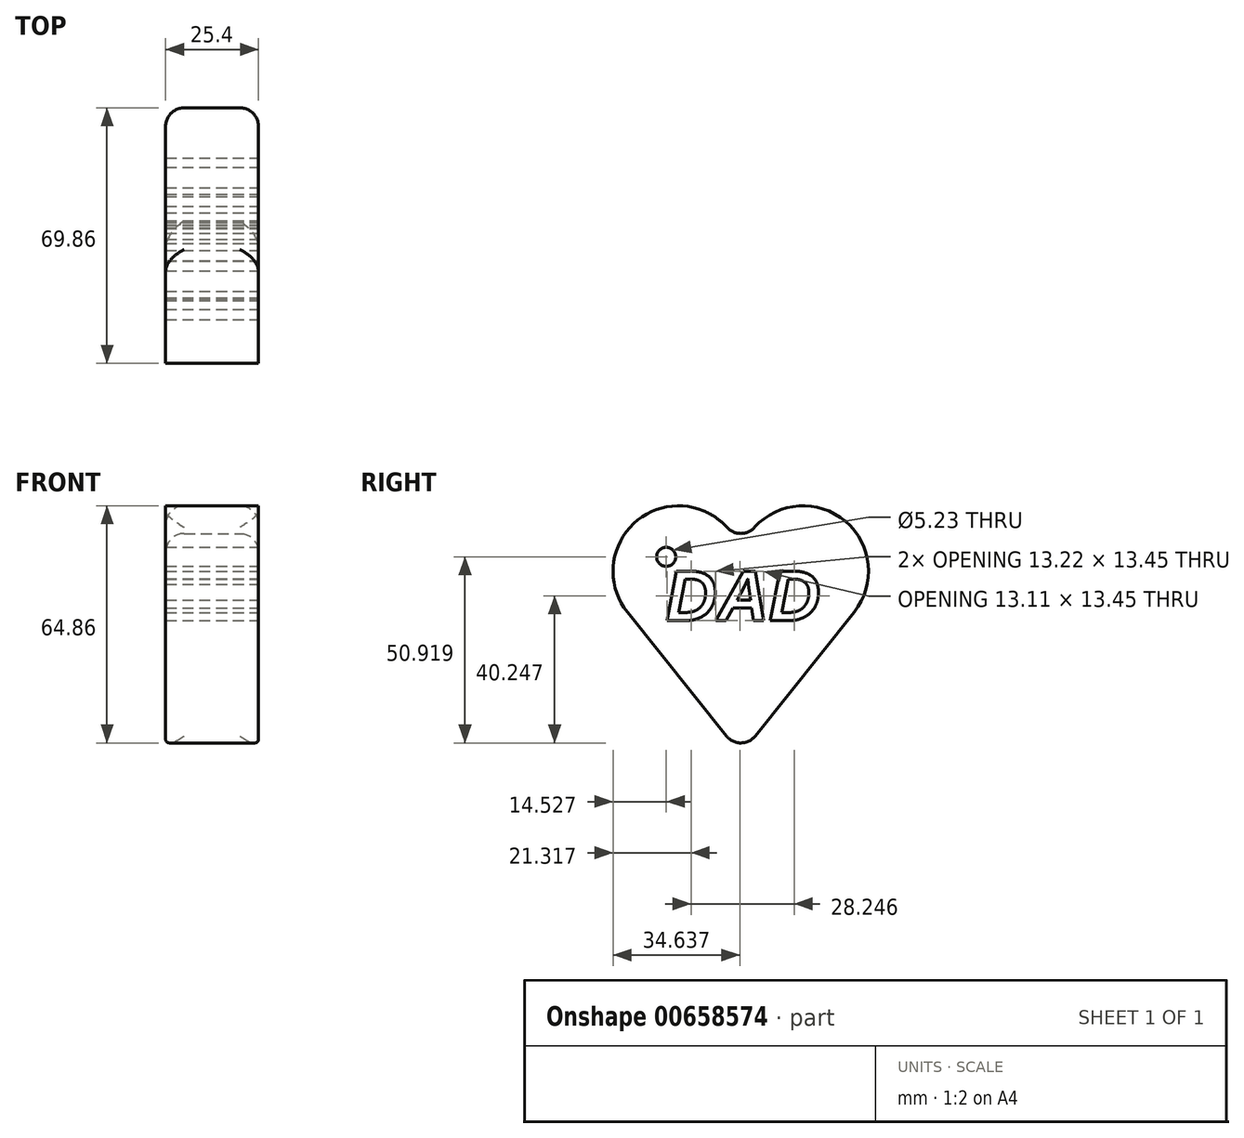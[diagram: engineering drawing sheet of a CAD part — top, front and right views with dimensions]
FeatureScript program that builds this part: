
annotation { "Feature Type Name" : "Feature", "Feature Type Description" : "" }
export const myFeature = defineFeature(function(context is Context, id is Id, definition is map)
    precondition{}
    {
        {
            var Q0;
            Q0=qCreatedBy(makeId("Right.planeOp"),FACE);
            var sketch = newSketch(context, id + "F0", { "sketchPlane" : qUnion([Q0])});
            skLineSegment(sketch, "E0", {"start": v(0, -38.87) * mm, "end": v(31.03, 0) * mm});
            skArc(sketch, "E1", {"start": v(31.03, 0) * mm, "mid": v(25.48, 26.94) * mm, "end": v(0, 16.6) * mm});
            skArc(sketch, "E2.MirrorCS", {"start": v(-31.03, 0) * mm, "mid": v(-25.48, 26.94) * mm, "end": v(0, 16.6) * mm});
            skLineSegment(sketch, "E3.MirrorCS", {"start": v(0, -38.87) * mm, "end": v(-31.03, 0) * mm});
            skSolve(sketch);
        }
        {
            var Q0;
            Q0=qSketchRegion(id+"F0",true);
            extrude(context, id + "F1", {"entities" : qUnion([Q0]), "depth" : 25.4 * mm, "offsetDistance" : 25.4 * mm});
        }
        {
            var Q0;
            Q0=makeQuery(id+"F1.opExtrude","CAP_FACE",FACE,{"disambiguationData":[OSD([sQuery(id+"F0.wireOp",EDGE,"E0"),sQuery(id+"F0.wireOp",EDGE,"E1"),sQuery(id+"F0.wireOp",EDGE,"E2.MirrorCS"),sQuery(id+"F0.wireOp",EDGE,"E3.MirrorCS")])],"isStart":false});
            var sketch = newSketch(context, id + "F2", { "sketchPlane" : qUnion([Q0])});
            skText(sketch, "E4", { "text": "DAD\n", "fontName": "Arimo-BoldItalic.ttf"});
            const initialGuessF2  = {"E4": [-0.02057, -0.00229, 1, 0, 0.01408]};
            skSetInitialGuess(sketch, initialGuessF2);
            skSolve(sketch);
        }
        {
            var Q0;
            Q0=qSketchRegion(id+"F2",true);
            extrude(context, id + "F3", {"entities" : qUnion([Q0]), "operationType" : NewBodyOperationType.REMOVE, "oppositeDirection" : true, "depth" : 152.4 * mm, "offsetDistance" : 25.4 * mm});
        }
        {
            var Q0;
            Q0=makeQuery(id+"F1.opExtrude","SWEPT_FACE",FACE,{"disambiguationData":[OSD([sQuery(id+"F0.wireOp",EDGE,"E1")])]});
            var Q1;
            Q1=makeQuery(id+"F1.opExtrude","SWEPT_EDGE",EDGE,{"disambiguationData":[OSD([sQuery(id+"F0.wireOp",EDGE,"E0"),sQuery(id+"F0.wireOp",EDGE,"E3.MirrorCS")])]});
            fillet(context, id + "F4", {"entities" : qUnion([Q0, Q1]), "radius" : 5.08 * mm, "tangentPropagation" : true, "allowEdgeOverflow" : false});
        }
        {
            var Q0;
            {var subQ0=sQuery(id+"F0.wireOp",EDGE,"E2.MirrorCS");var subQ1=sQuery(id+"F0.wireOp",EDGE,"E0");var subQ2=sQuery(id+"F0.wireOp",EDGE,"E3.MirrorCS");var subQ3=sQuery(id+"F0.wireOp",EDGE,"E1");Q0=makeQuery(id+"F3.boolean.opBoolean","SPLIT",FACE,{"disambiguationData":[TD([makeQuery(id+"F1.opExtrude","SWEPT_FACE",FACE,{"disambiguationData":[OSD([subQ1])]})])],"derivedFrom":makeQuery(id+"F1.opExtrude","CAP_FACE",FACE,{"disambiguationData":[OSD([subQ1,subQ3,subQ0,subQ2])],"isStart":false})});}
            var sketch = newSketch(context, id + "F5", { "sketchPlane" : qUnion([Q0])});
            skCircle(sketch, "E5", {"center": v(-20.4, 15.1) * mm, "radius": 2.62 * mm});
            skSolve(sketch);
        }
        {
            var Q0;
            Q0=makeQuery(id+"F5.imprint","IMPRINT",FACE,{"disambiguationData":[TD([[makeQuery(id+"F5.imprint","IMPRINT",EDGE,{"derivedFrom":sQuery(id+"F5.wireOp",EDGE,"E5")}),1.0]])]});
            extrude(context, id + "F6", {"entities" : qUnion([Q0]), "operationType" : NewBodyOperationType.REMOVE, "oppositeDirection" : true, "depth" : 152.4 * mm, "offsetDistance" : 25.4 * mm});
        }
    });
